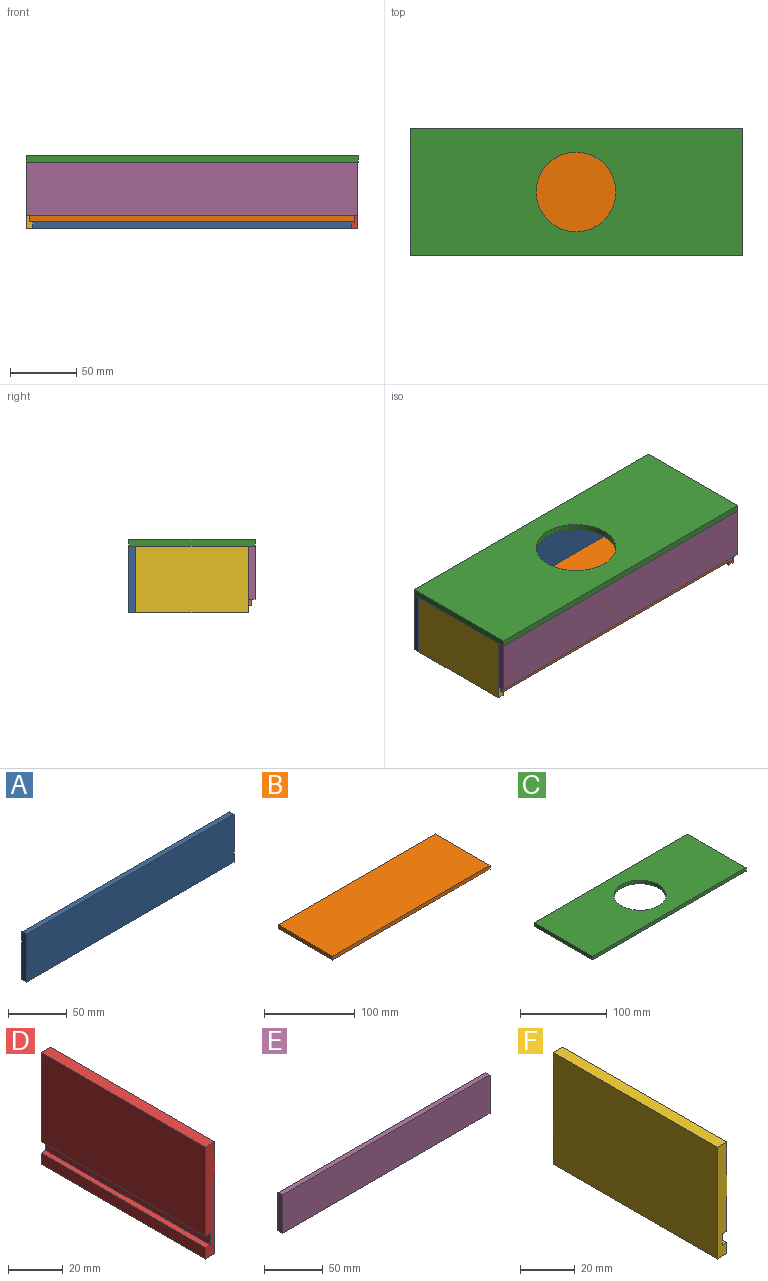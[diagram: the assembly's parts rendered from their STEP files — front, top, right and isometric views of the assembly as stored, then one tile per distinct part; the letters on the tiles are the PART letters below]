
ASSEMBLY  parts=6 mates=5
PART A: 6 faces, bbox 250x5x50 mm
  f0: plane 250x5mm, normal (0,0,1), area 1250mm2, adj f1,f3,f4,f5
  f1: plane 50x5mm, normal (-1,0,0), area 250mm2, adj f0,f2,f4,f5
  f2: plane 250x5mm, normal (0,0,-1), area 1250mm2, adj f1,f3,f4,f5
  f3: plane 50x5mm, normal (1,0,0), area 250mm2, adj f0,f2,f4,f5
  f4: plane 250x50mm, normal (0,-1,0), area 12500mm2, adj f0,f1,f2,f3
  f5: plane 250x50mm, normal (0,1,0), area 12500mm2, adj f0,f1,f2,f3
PART B: 6 faces, bbox 245x85x5 mm
  f0: plane 245x5mm, normal (0,1,0), area 1225mm2, adj f1,f3,f4,f5
  f1: plane 85x5mm, normal (-1,0,0), area 425mm2, adj f0,f2,f4,f5
  f2: plane 245x5mm, normal (0,-1,0), area 1225mm2, adj f1,f3,f4,f5
  f3: plane 85x5mm, normal (1,0,0), area 425mm2, adj f0,f2,f4,f5
  f4: plane 245x85mm, normal (0,0,1), area 20825mm2, adj f0,f1,f2,f3
  f5: plane 245x85mm, normal (0,0,-1), area 20825mm2, adj f0,f1,f2,f3
PART C: 7 faces, bbox 250x95x5 mm
  f0: plane 250x5mm, normal (0,1,0), area 1250mm2, adj f1,f4,f5,f6
  f1: plane 95x5mm, normal (-1,0,0), area 475mm2, adj f0,f2,f5,f6
  f2: plane 250x5mm, normal (0,-1,0), area 1250mm2, adj f1,f4,f5,f6
  f3: cylinder r=30mm len=60mm, axis (0,0,-1), area 942.5mm2, adj f5,f6
  f4: plane 95x5mm, normal (1,0,0), area 475mm2, adj f0,f2,f5,f6
  f5: plane 250x95mm, normal (0,0,1), area 20922.6mm2, adj f0,f1,f2,f3,f4
  f6: plane 250x95mm, normal (0,0,-1), area 20922.6mm2, adj f0,f1,f2,f3,f4
PART D: 10 faces, bbox 5x85x50 mm
  f0: plane 85x5mm, normal (-1,0,0), area 425mm2, adj f1,f3,f4,f7
  f1: plane 50x5mm, normal (0,1,0), area 237.5mm2, adj f0,f2,f4,f5,f6,f7,f8,f9
  f2: plane 85x5mm, normal (0,0,1), area 425mm2, adj f1,f3,f5,f6
  f3: plane 50x5mm, normal (0,-1,0), area 237.5mm2, adj f0,f2,f4,f5,f6,f7,f8,f9
  f4: plane 85x5mm, normal (0,0,-1), area 425mm2, adj f0,f1,f3,f5
  f5: plane 85x50mm, normal (1,0,0), area 4250mm2, adj f1,f2,f3,f4
  f6: plane 85x40mm, normal (-1,0,0), area 3400mm2, adj f1,f2,f3,f8
  f7: plane 85x2.5mm, normal (0,0,1), area 212.5mm2, adj f0,f1,f3,f9
  f8: plane 85x2.5mm, normal (0,0,-1), area 212.5mm2, adj f1,f3,f6,f9
  f9: plane 85x5mm, normal (-1,0,0), area 425mm2, adj f1,f3,f7,f8
PART E: 6 faces, bbox 250x5x40 mm
  f0: plane 250x5mm, normal (0,0,1), area 1250mm2, adj f1,f3,f4,f5
  f1: plane 40x5mm, normal (-1,0,0), area 200mm2, adj f0,f2,f4,f5
  f2: plane 250x5mm, normal (0,0,-1), area 1250mm2, adj f1,f3,f4,f5
  f3: plane 40x5mm, normal (1,0,0), area 200mm2, adj f0,f2,f4,f5
  f4: plane 250x40mm, normal (0,-1,0), area 10000mm2, adj f0,f1,f2,f3
  f5: plane 250x40mm, normal (0,1,0), area 10000mm2, adj f0,f1,f2,f3
PART F: 10 faces, bbox 5x85x50 mm
  f0: plane 85x40mm, normal (1,0,0), area 3400mm2, adj f1,f2,f3,f8
  f1: plane 50x5mm, normal (0,1,0), area 237.5mm2, adj f0,f2,f4,f5,f6,f7,f8,f9
  f2: plane 85x5mm, normal (0,0,1), area 425mm2, adj f0,f1,f3,f6
  f3: plane 50x5mm, normal (0,-1,0), area 237.5mm2, adj f0,f2,f4,f5,f6,f7,f8,f9
  f4: plane 85x5mm, normal (0,0,-1), area 425mm2, adj f1,f3,f5,f6
  f5: plane 85x5mm, normal (1,0,0), area 425mm2, adj f1,f3,f4,f7
  f6: plane 85x50mm, normal (-1,0,0), area 4250mm2, adj f1,f2,f3,f4
  f7: plane 85x2.5mm, normal (0,0,1), area 212.5mm2, adj f1,f3,f5,f9
  f8: plane 85x2.5mm, normal (0,0,-1), area 212.5mm2, adj f0,f1,f3,f9
  f9: plane 85x5mm, normal (1,0,0), area 425mm2, adj f1,f3,f7,f8
PLACE A t=(-76.71,99.17,10.65)mm
PLACE B t=(-72.93,70.13,-76.75)mm
PLACE C t=(106.09,51.67,-31.75)mm
PLACE D t=(41.49,54.14,-41.2)mm
PLACE E t=(-73.57,9.17,40.33)mm
PLACE F t=(-203.51,44.87,-55.74)mm
MATE fastened F.f3 <-> E.f5  axis (0,-1,0) through (-203.51,9.17,-31.75)mm
MATE fastened C.f6 <-> E.f0  axis (0,0,-1) through (46.49,4.17,-31.75)mm
MATE fastened D.f3 <-> E.f5  axis (0,-1,0) through (46.49,9.17,-31.75)mm
MATE pin_slot B.f3 <-> D.f9  axis (1,0,0) through (43.99,49.62,-74.25)mm
MATE fastened A.f4 <-> D.f1  axis (0,-1,0) through (46.49,94.17,-31.75)mm
